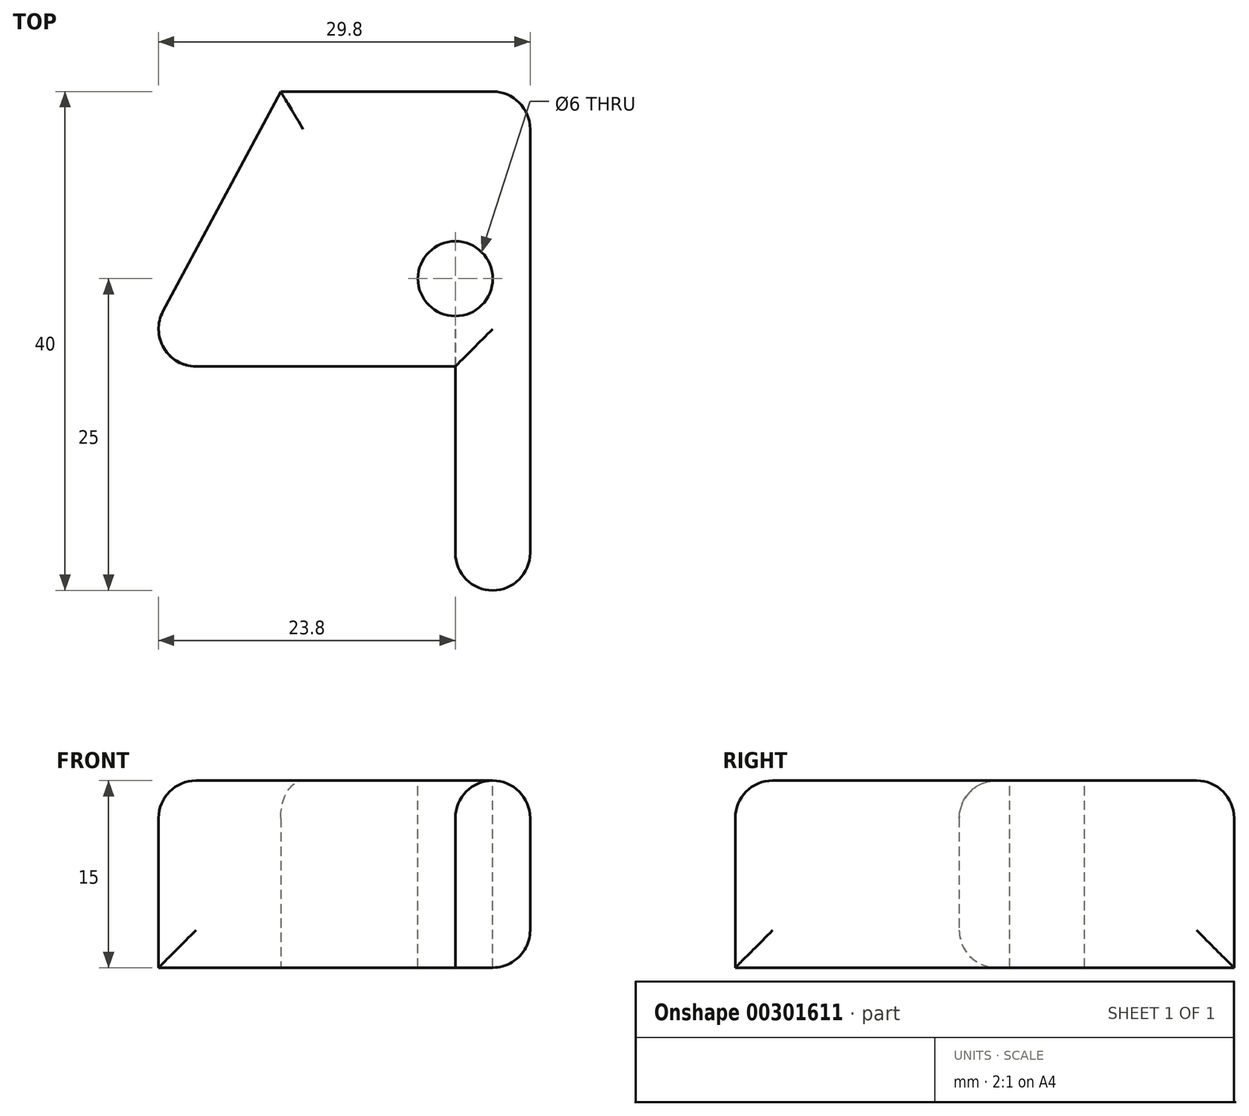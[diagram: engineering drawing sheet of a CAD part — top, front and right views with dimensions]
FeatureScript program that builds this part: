
annotation { "Feature Type Name" : "Feature", "Feature Type Description" : "" }
export const myFeature = defineFeature(function(context is Context, id is Id, definition is map)
    precondition{}
    {
        {
            var Q0;
            Q0=qCreatedBy(makeId("Top.planeOp"),FACE);
            var sketch = newSketch(context, id + "F0", { "sketchPlane" : qUnion([Q0])});
            skLineSegment(sketch, "E0", {"start": v(0, 0) * mm, "end": v(0, 40) * mm});
            skLineSegment(sketch, "E1", {"start": v(0, 40) * mm, "end": v(-20, 40) * mm});
            skLineSegment(sketch, "E2", {"start": v(-20, 40) * mm, "end": v(-31.8, 17.96) * mm});
            skLineSegment(sketch, "E3", {"start": v(-31.8, 17.96) * mm, "end": v(-6, 17.96) * mm});
            skLineSegment(sketch, "E4", {"start": v(-6, 17.96) * mm, "end": v(-6, 0) * mm});
            skLineSegment(sketch, "E5", {"start": v(-6, 0) * mm, "end": v(0, 0) * mm});
            skSolve(sketch);
        }
        {
            var Q0;
            Q0 = qSketchRegion(id + "F0", true);
            extrude(context, id + "F1", {"entities" : qUnion([Q0]), "depth" : 15 * mm});
        }
        {
            var Q0;
            Q0=makeQuery(id+"F1.opExtrude","CAP_FACE",FACE,{"disambiguationData":[OSD([sQuery(id+"F0.wireOp",EDGE,"E0"),sQuery(id+"F0.wireOp",EDGE,"E1"),sQuery(id+"F0.wireOp",EDGE,"E2"),sQuery(id+"F0.wireOp",EDGE,"E3"),sQuery(id+"F0.wireOp",EDGE,"E4"),sQuery(id+"F0.wireOp",EDGE,"E5")])],"isStart":false});
            var sketch = newSketch(context, id + "F2", { "sketchPlane" : qUnion([Q0])});
            skCircle(sketch, "E6", {"center": v(-6, 25) * mm, "radius": 3 * mm});
            skSolve(sketch);
        }
        {
            var Q0;
            Q0 = qSketchRegion(id + "F2", true);
            extrude(context, id + "F3", {"entities" : qUnion([Q0]), "operationType" : NewBodyOperationType.REMOVE, "oppositeDirection" : true, "depth" : 25 * mm});
        }
        {
            var Q0;
            Q0=makeQuery(id+"F1.opExtrude","CAP_EDGE",EDGE,{"disambiguationData":[OSD([sQuery(id+"F0.wireOp",EDGE,"E0")])],"isStart":false});
            var Q1;
            Q1=makeQuery(id+"F1.opExtrude","CAP_EDGE",EDGE,{"disambiguationData":[OSD([sQuery(id+"F0.wireOp",EDGE,"E4")])],"isStart":false});
            var Q2;
            Q2=makeQuery(id+"F1.opExtrude","CAP_EDGE",EDGE,{"disambiguationData":[OSD([sQuery(id+"F0.wireOp",EDGE,"E3")])],"isStart":false});
            var Q3;
            Q3=makeQuery(id+"F1.opExtrude","CAP_EDGE",EDGE,{"disambiguationData":[OSD([sQuery(id+"F0.wireOp",EDGE,"E2")])],"isStart":false});
            var Q4;
            Q4=makeQuery(id+"F1.opExtrude","CAP_EDGE",EDGE,{"disambiguationData":[OSD([sQuery(id+"F0.wireOp",EDGE,"E1")])],"isStart":false});
            var Q5;
            Q5=makeQuery(id+"F1.opExtrude","SWEPT_EDGE",EDGE,{"disambiguationData":[OSD([sQuery(id+"F0.wireOp",EDGE,"E0"),sQuery(id+"F0.wireOp",EDGE,"E1")])]});
            var Q6;
            Q6=makeQuery(id+"F1.opExtrude","CAP_EDGE",EDGE,{"disambiguationData":[OSD([sQuery(id+"F0.wireOp",EDGE,"E5")])],"isStart":false});
            var Q7;
            Q7=makeQuery(id+"F1.opExtrude","SWEPT_EDGE",EDGE,{"disambiguationData":[OSD([sQuery(id+"F0.wireOp",EDGE,"E0"),sQuery(id+"F0.wireOp",EDGE,"E5")])]});
            var Q8;
            Q8=makeQuery(id+"F1.opExtrude","CAP_EDGE",EDGE,{"disambiguationData":[OSD([sQuery(id+"F0.wireOp",EDGE,"E0")])],"isStart":true});
            var Q9;
            Q9=makeQuery(id+"F1.opExtrude","CAP_EDGE",EDGE,{"disambiguationData":[OSD([sQuery(id+"F0.wireOp",EDGE,"E3")])],"isStart":true});
            var Q10;
            Q10=makeQuery(id+"F1.opExtrude","SWEPT_EDGE",EDGE,{"disambiguationData":[OSD([sQuery(id+"F0.wireOp",EDGE,"E2"),sQuery(id+"F0.wireOp",EDGE,"E3")])]});
            var Q11;
            Q11=makeQuery(id+"F1.opExtrude","SWEPT_EDGE",EDGE,{"disambiguationData":[OSD([sQuery(id+"F0.wireOp",EDGE,"E4"),sQuery(id+"F0.wireOp",EDGE,"E5")])]});
            fillet(context, id + "F4", {"entities" : qUnion([Q0, Q1, Q2, Q3, Q4, Q5, Q6, Q7, Q8, Q9, Q10, Q11]), "radius" : 3 * mm, "tangentPropagation" : true, "allowEdgeOverflow" : false});
        }
    });
